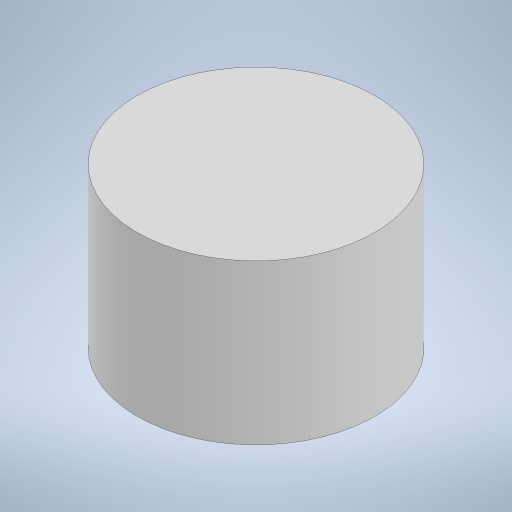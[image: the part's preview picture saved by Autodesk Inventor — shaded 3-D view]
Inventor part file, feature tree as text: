
AUTODESK INVENTOR PART (.ipt)
format: ipt  version: 2024.2 (Build 282272000, 272)  size: 178,176 bytes
history: native  units: in
note: dims shown in document units (in); Inventor stores cm internally (conversion verified against a paired STEP export)
features: extrude x1, sketch x1
ambient origin geometry x8: Origin, YZ Plane, XZ Plane, XY Plane, X Axis, Y Axis, Z Axis, Center Point
bodies: Solid1 (feature_tree)
feature tree (2):
  extrude  "Extrusion1"  Depth=2.0in TaperAngle=0.0deg
  sketch  "Sketch1"  dims[d0=2.98in d1=2.0in d2=0.0in]
